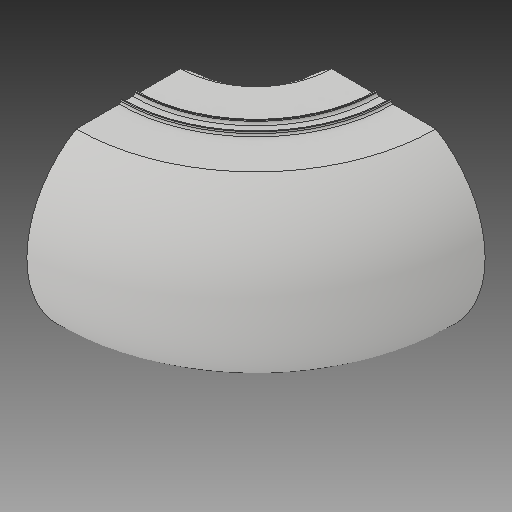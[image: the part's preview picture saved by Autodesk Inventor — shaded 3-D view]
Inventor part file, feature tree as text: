
AUTODESK INVENTOR PART (.ipt)
format: ipt  version: 2017 (Build 210142000, 142)  size: 189,440 bytes
history: native  units: in
note: dims shown in document units (in); Inventor stores cm internally (conversion verified against a paired STEP export)
features: other x1, delete_face x1, sketch x1
ambient origin geometry x8: Origin, YZ Plane, XZ Plane, XY Plane, X Axis, Y Axis, Z Axis, Center Point
bodies: Solid1 (feature_tree)
feature tree (3):
  other  "corridor"
  delete_face  "Delete Face2"
  sketch  "Sketch1"  dims[d1=4.0in d2=90.0deg d16=0.5833in d17=0.0625in d18=0.0625in d19=0.125in d28=45.0deg d31=3.8873in d34=2.0in d37=0.25in d38=0.125in d40=0.0884in d41=45.0deg]
